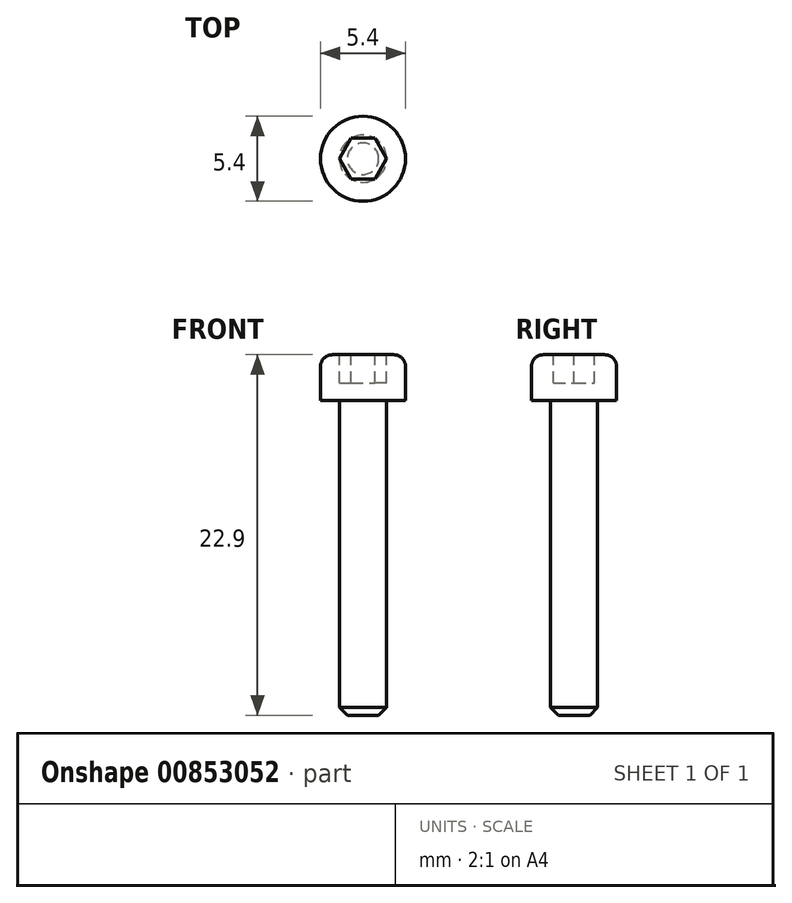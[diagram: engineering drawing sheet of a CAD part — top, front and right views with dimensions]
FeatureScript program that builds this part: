
annotation { "Feature Type Name" : "Feature", "Feature Type Description" : "" }
export const myFeature = defineFeature(function(context is Context, id is Id, definition is map)
    precondition{}
    {
        {
            var Q0;
            Q0=qCreatedBy(makeId("Front.planeOp"),FACE);
            var sketch = newSketch(context, id + "F0", { "sketchPlane" : qUnion([Q0])});
            skLineSegment(sketch, "E0", {"start": v(0, 0) * mm, "end": v(0, 22.9) * mm});
            skLineSegment(sketch, "E1", {"start": v(0, 22.9) * mm, "end": v(2.7, 22.9) * mm});
            skLineSegment(sketch, "E2", {"start": v(2.7, 22.9) * mm, "end": v(2.7, 20) * mm});
            skLineSegment(sketch, "E3", {"start": v(2.7, 20) * mm, "end": v(1.5, 20) * mm});
            skLineSegment(sketch, "E4", {"start": v(1.5, 20) * mm, "end": v(1.5, 0) * mm});
            skLineSegment(sketch, "E5", {"start": v(1.5, 0) * mm, "end": v(0, 0) * mm});
            skSolve(sketch);
        }
        {
            var Q0;
            Q0 = qSketchRegion(id + "F0", true);
            var Q1;
            Q1=sQuery(id+"F0.wireOp",EDGE,"E0");
            revolve(context, id + "F1", {"surfaceOperationType" : NewSurfaceOperationType.NEW, "entities" : qUnion([Q0]), "axis" : qUnion([Q1]), "revolveType" : RevolveType.FULL});
        }
        {
            var Q0;
            Q0=makeQuery(id+"F1.opRevolve","SWEPT_FACE",FACE,{"disambiguationData":[OSD([sQuery(id+"F0.wireOp",EDGE,"E1")])]});
            var sketch = newSketch(context, id + "F2", { "sketchPlane" : qUnion([Q0])});
            skCircle(sketch, "E6.cCircle", {"center": v(0, 0) * mm, "radius": 1.3 * mm, "construction": true});
            skLineSegment(sketch, "E6.0", {"start": v(-0.75, 1.3) * mm, "end": v(0.75, 1.3) * mm});
            skLineSegment(sketch, "E6.1", {"start": v(0.75, 1.3) * mm, "end": v(1.5, 0) * mm});
            skLineSegment(sketch, "E6.2", {"start": v(1.5, 0) * mm, "end": v(0.75, -1.3) * mm});
            skLineSegment(sketch, "E6.3", {"start": v(0.75, -1.3) * mm, "end": v(-0.75, -1.3) * mm});
            skLineSegment(sketch, "E6.4", {"start": v(-0.75, -1.3) * mm, "end": v(-1.5, 0) * mm});
            skLineSegment(sketch, "E6.5", {"start": v(-1.5, 0) * mm, "end": v(-0.75, 1.3) * mm});
            skPoint(sketch, "E6.0.midPoint", {"position": v(0, 1.3) * mm});
            skSolve(sketch);
        }
        {
            var Q0;
            Q0 = qSketchRegion(id + "F2", true);
            extrude(context, id + "F3", {"entities" : qUnion([Q0]), "operationType" : NewBodyOperationType.REMOVE, "oppositeDirection" : true, "depth" : 1.8 * mm, "offsetDistance" : 25 * mm});
        }
        {
            var Q0;
            Q0=makeQuery(id+"F1.opRevolve","SWEPT_EDGE",EDGE,{"disambiguationData":[OSD([sQuery(id+"F0.wireOp",EDGE,"E1"),sQuery(id+"F0.wireOp",EDGE,"E2")])]});
            fillet(context, id + "F4", {"entities" : qUnion([Q0]), "radius" : 0.75 * mm, "tangentPropagation" : true, "allowEdgeOverflow" : false});
        }
        {
            var Q0;
            Q0=makeQuery(id+"F1.opRevolve","SWEPT_EDGE",EDGE,{"disambiguationData":[OSD([sQuery(id+"F0.wireOp",EDGE,"E4"),sQuery(id+"F0.wireOp",EDGE,"E5")])]});
            chamfer(context, id + "F5", {"entities" : qUnion([Q0]), "width" : 0.5 * mm, "tangentPropagation" : true});
        }
    });
